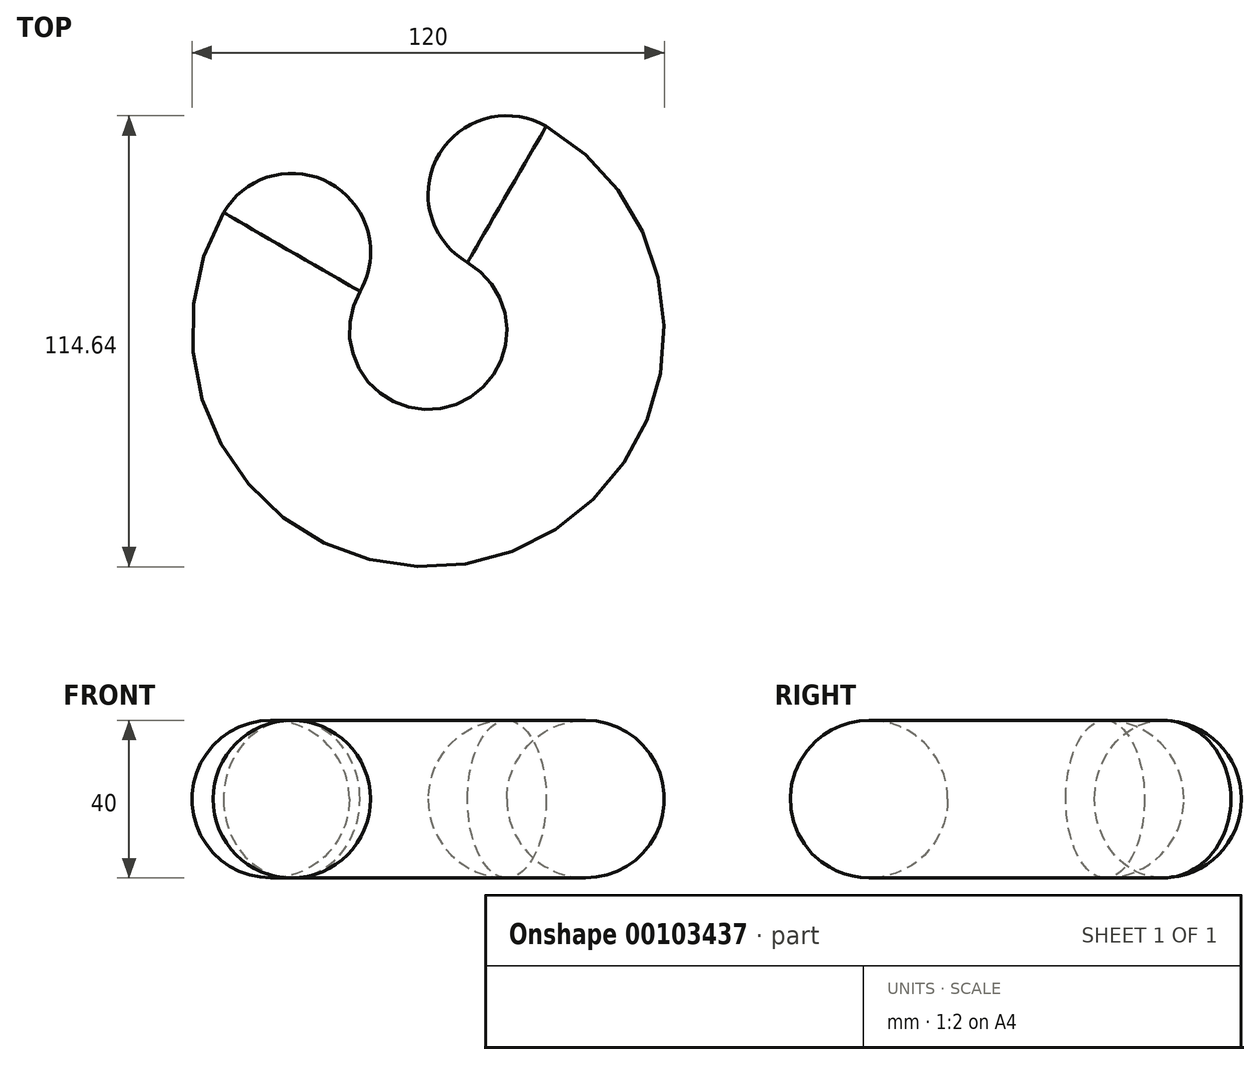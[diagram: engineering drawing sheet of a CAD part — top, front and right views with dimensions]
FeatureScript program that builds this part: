
annotation { "Feature Type Name" : "Feature", "Feature Type Description" : "" }
export const myFeature = defineFeature(function(context is Context, id is Id, definition is map)
    precondition{}
    {
        {
            var Q0;
            Q0=qCreatedBy(makeId("Top.planeOp"),FACE);
            var sketch = newSketch(context, id + "F0", { "sketchPlane" : qUnion([Q0])});
            skArc(sketch, "E0", {"start": v(-20, 34.64) * mm, "mid": v(10.35, -38.64) * mm, "end": v(0, 40) * mm});
            skLineSegment(sketch, "E1", {"start": v(0, 0) * mm, "end": v(-31.54, 54.62) * mm, "construction": true});
            skLineSegment(sketch, "E2", {"start": v(0, 0) * mm, "end": v(0, 63.07) * mm, "construction": true});
            skSolve(sketch);
        }
        {
            var Q0;
            Q0=sQuery(id+"F0.wireOp",EDGE,"E1");
            cPlane(context, id + "F1", {"entities" : qUnion([Q0]), "cplaneType" : CPlaneType.LINE_ANGLE, "offset" : 150 * mm, "angle" : 90 * degree, "width" : 150 * mm, "height" : 150 * mm});
        }
        {
            var Q0;
            Q0=qCreatedBy(id+"F1.planeOp",FACE);
            var sketch = newSketch(context, id + "F2", { "sketchPlane" : qUnion([Q0])});
            skCircle(sketch, "E3", {"center": v(40, 0) * mm, "radius": 20 * mm});
            skSolve(sketch);
        }
        {
            var Q0;
            Q0=makeQuery(id+"F2.imprint","IMPRINT",FACE,{"disambiguationData":[TD([[makeQuery(id+"F2.imprint","IMPRINT",EDGE,{"derivedFrom":sQuery(id+"F2.wireOp",EDGE,"E3")}),1.0]])]});
            var Q1;
            Q1=sQuery(id+"F0.wireOp",EDGE,"E0");
            sweep(context, id + "F3", {"profiles" : qUnion([Q0]), "path" : qUnion([Q1])});
        }
        {
            var Q0;
            Q0=makeQuery(id+"F3.opSweep","CAP_FACE",FACE,{"disambiguationData":[OSD([sQuery(id+"F0.wireOp",VERTEX,"E0.start"),sQuery(id+"F2.wireOp",EDGE,"E3")])],"isStart":true});
            var Q1;
            Q1=makeQuery(id+"F3.opSweep","CAP_FACE",FACE,{"disambiguationData":[OSD([sQuery(id+"F0.wireOp",VERTEX,"E0.end"),sQuery(id+"F2.wireOp",EDGE,"E3")])],"isStart":false});
            fillet(context, id + "F4", {"entities" : qUnion([Q0, Q1]), "radius" : 20 * mm, "allowEdgeOverflow" : false});
        }
    });
